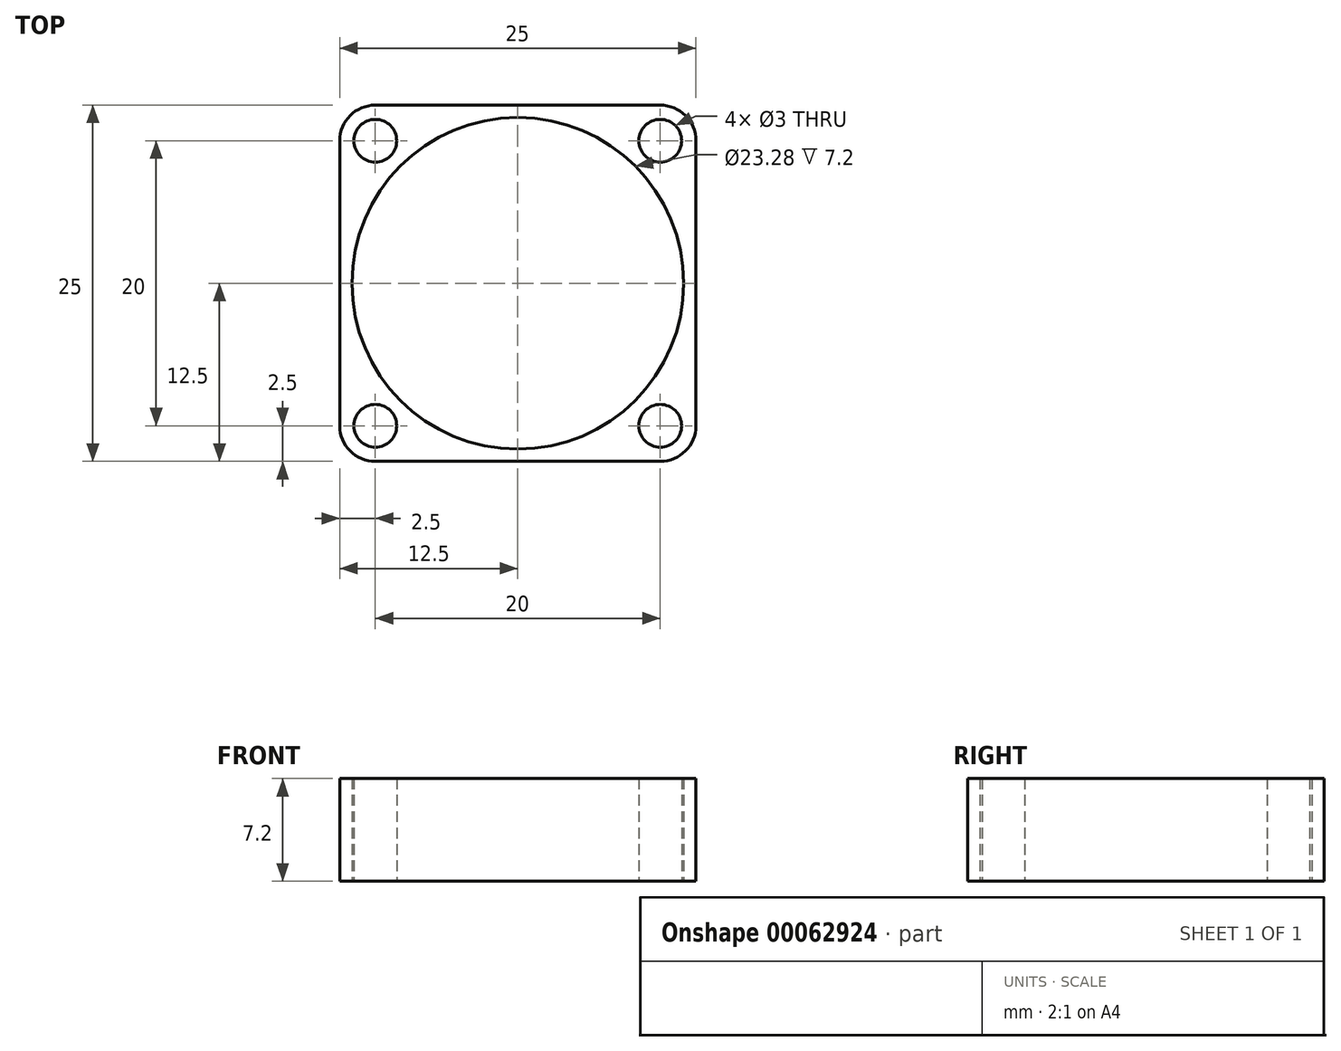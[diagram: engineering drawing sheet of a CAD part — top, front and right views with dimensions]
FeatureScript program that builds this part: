
annotation { "Feature Type Name" : "Feature", "Feature Type Description" : "" }
export const myFeature = defineFeature(function(context is Context, id is Id, definition is map)
    precondition{}
    {
        {
            var Q0;
            Q0=qCreatedBy(makeId("Top.planeOp"),FACE);
            var sketch = newSketch(context, id + "F0", { "sketchPlane" : qUnion([Q0])});
            skLineSegment(sketch, "E0.bottom", {"start": v(2.5, 0) * mm, "end": v(22.5, 0) * mm});
            skLineSegment(sketch, "E0.top", {"start": v(2.5, 25) * mm, "end": v(22.5, 25) * mm});
            skLineSegment(sketch, "E0.left", {"start": v(0, 2.5) * mm, "end": v(0, 22.5) * mm});
            skLineSegment(sketch, "E0.right", {"start": v(25, 2.5) * mm, "end": v(25, 22.5) * mm});
            skLineSegment(sketch, "E1.bottom", {"start": v(2.5, 2.5) * mm, "end": v(22.5, 2.5) * mm, "construction": true});
            skLineSegment(sketch, "E1.top", {"start": v(2.5, 22.5) * mm, "end": v(22.5, 22.5) * mm, "construction": true});
            skLineSegment(sketch, "E1.left", {"start": v(2.5, 2.5) * mm, "end": v(2.5, 22.5) * mm, "construction": true});
            skLineSegment(sketch, "E1.right", {"start": v(22.5, 2.5) * mm, "end": v(22.5, 22.5) * mm, "construction": true});
            skPoint(sketch, "E2", {"position": v(12.5, 12.5) * mm});
            skPoint(sketch, "E2.positionSnap0", {"position": v(2.5, 12.5) * mm});
            skPoint(sketch, "E2.positionSnap1", {"position": v(12.5, 22.5) * mm});
            skPoint(sketch, "E3.positionSnap0", {"position": v(0, 12.5) * mm});
            skPoint(sketch, "E3.positionSnap1", {"position": v(12.5, 25) * mm});
            skCircle(sketch, "E4", {"center": v(2.5, 22.5) * mm, "radius": 1.5 * mm});
            skCircle(sketch, "E5", {"center": v(22.5, 22.5) * mm, "radius": 1.5 * mm});
            skCircle(sketch, "E6", {"center": v(22.5, 2.5) * mm, "radius": 1.5 * mm});
            skCircle(sketch, "E7", {"center": v(2.5, 2.5) * mm, "radius": 1.5 * mm});
            skPoint(sketch, "E8.visualSharp", {"position": v(0, 25) * mm});
            skArc(sketch, "E8.filletArc", {"start": v(2.5, 25) * mm, "mid": v(0.73, 24.27) * mm, "end": v(0, 22.5) * mm});
            skPoint(sketch, "E9.visualSharp", {"position": v(25, 25) * mm});
            skArc(sketch, "E9.filletArc", {"start": v(25, 22.5) * mm, "mid": v(24.27, 24.27) * mm, "end": v(22.5, 25) * mm});
            skPoint(sketch, "E10.visualSharp", {"position": v(25, 0) * mm});
            skArc(sketch, "E10.filletArc", {"start": v(22.5, 0) * mm, "mid": v(24.27, 0.73) * mm, "end": v(25, 2.5) * mm});
            skPoint(sketch, "E11.visualSharp", {"position": v(0, 0) * mm});
            skArc(sketch, "E11.filletArc", {"start": v(0, 2.5) * mm, "mid": v(0.73, 0.73) * mm, "end": v(2.5, 0) * mm});
            skCircle(sketch, "E12", {"center": v(12.5, 12.5) * mm, "radius": 11.64 * mm});
            skSolve(sketch);
        }
        {
            var Q0;
            Q0 = qSketchRegion(id + "F0", true);
            extrude(context, id + "F1", {"entities" : qUnion([Q0]), "depth" : 7.2 * mm});
        }
    });
